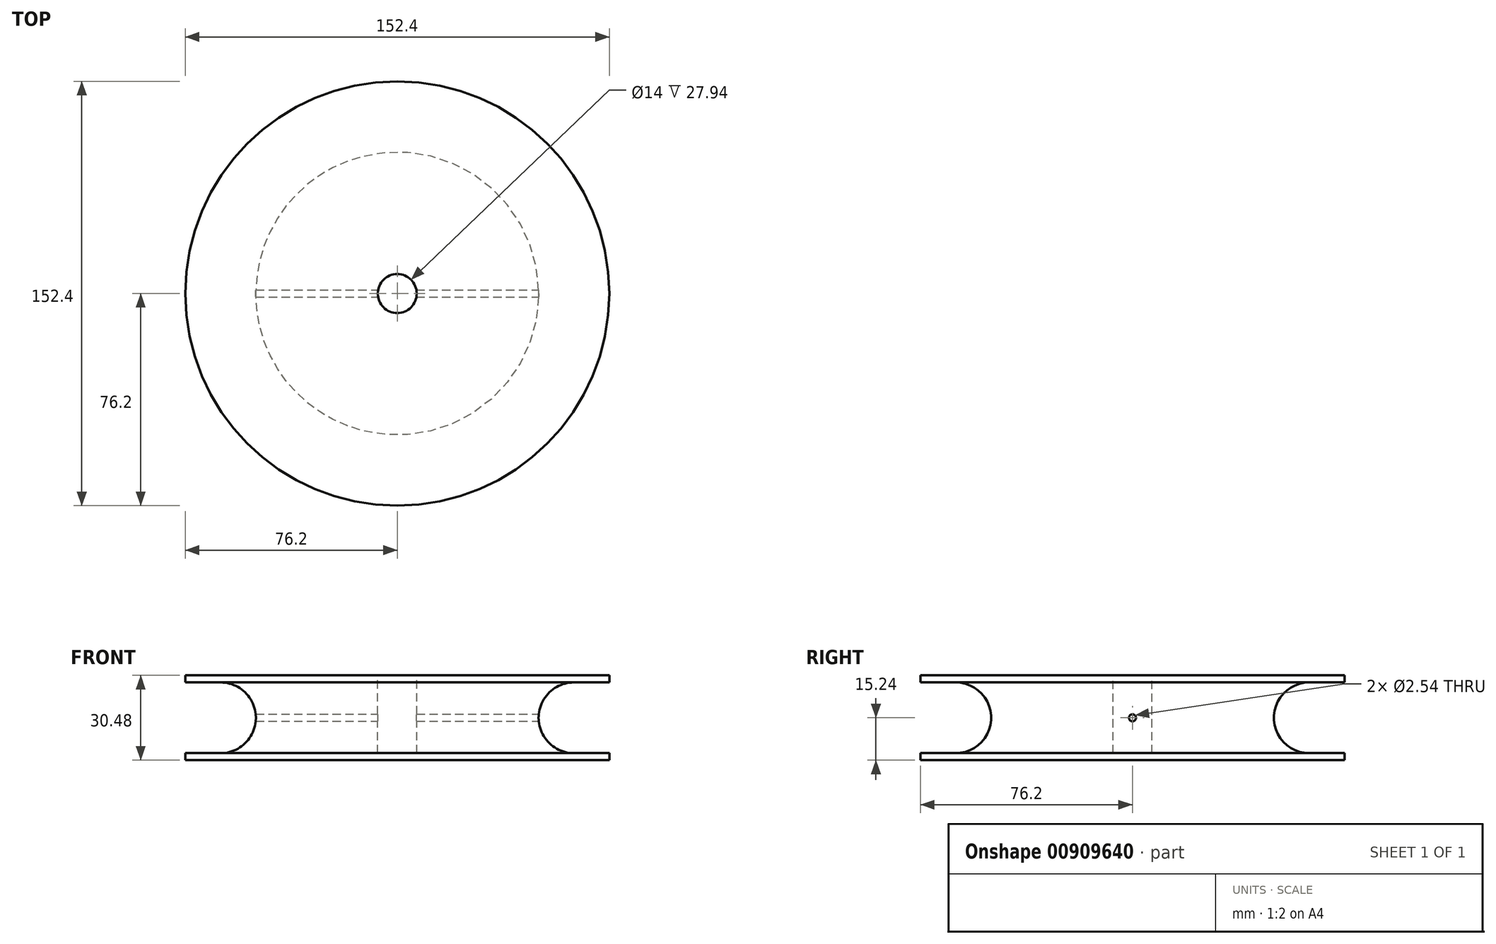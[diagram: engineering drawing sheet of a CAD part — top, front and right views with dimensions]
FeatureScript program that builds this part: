
annotation { "Feature Type Name" : "Feature", "Feature Type Description" : "" }
export const myFeature = defineFeature(function(context is Context, id is Id, definition is map)
    precondition{}
    {
        {
            var Q0;
            Q0=qCreatedBy(makeId("Top.planeOp"),FACE);
            var sketch = newSketch(context, id + "F0", { "sketchPlane" : qUnion([Q0])});
            skCircle(sketch, "E0", {"center": v(0, 0) * mm, "radius": 50.8 * mm});
            skCircle(sketch, "E1", {"center": v(0, 0) * mm, "radius": 76.2 * mm});
            skSolve(sketch);
        }
        {
            var Q0;
            Q0=makeQuery(id+"F0.imprint","IMPRINT",FACE,{"disambiguationData":[TD([[makeQuery(id+"F0.imprint","IMPRINT",EDGE,{"derivedFrom":sQuery(id+"F0.wireOp",EDGE,"E0")}),1.0]])]});
            extrude(context, id + "F1", {"entities" : qUnion([Q0]), "depth" : 30.48 * mm, "offsetDistance" : 25.4 * mm});
        }
        {
            var Q0;
            Q0=qSketchRegion(id+"F0",true);
            extrude(context, id + "F2", {"entities" : qUnion([Q0]), "operationType" : NewBodyOperationType.ADD, "depth" : 2.54 * mm, "offsetDistance" : 25.4 * mm});
        }
        {
            var Q0;
            Q0=makeQuery(id+"F1.opExtrude","CAP_FACE",FACE,{"disambiguationData":[OSD([sQuery(id+"F0.wireOp",EDGE,"E0")])],"isStart":false});
            var sketch = newSketch(context, id + "F3", { "sketchPlane" : qUnion([Q0])});
            skCircle(sketch, "E2", {"center": v(0, 0) * mm, "radius": 76.2 * mm});
            skSolve(sketch);
        }
        {
            var Q0;
            Q0=qSketchRegion(id+"F3",true);
            extrude(context, id + "F4", {"entities" : qUnion([Q0]), "operationType" : NewBodyOperationType.ADD, "depth" : -2.54 * mm, "offsetDistance" : 25.4 * mm});
        }
        {
            var Q0;
            Q0=makeQuery(id+"F1.opExtrude","SWEPT_FACE",FACE,{"disambiguationData":[OSD([sQuery(id+"F0.wireOp",EDGE,"E0")])]});
            fillet(context, id + "F5", {"entities" : qUnion([Q0]), "radius" : 12.7 * mm, "tangentPropagation" : true, "allowEdgeOverflow" : false});
        }
        {
            var Q0;
            Q0=qCreatedBy(makeId("Right.planeOp"),FACE);
            var sketch = newSketch(context, id + "F6", { "sketchPlane" : qUnion([Q0])});
            skLineSegment(sketch, "E3", {"start": v(0, 0) * mm, "end": v(0, 15.24) * mm, "construction": true});
            skCircle(sketch, "E4", {"center": v(0, 15.24) * mm, "radius": 1.27 * mm});
            skSolve(sketch);
        }
        {
            var Q0;
            Q0=qSketchRegion(id+"F6",true);
            extrude(context, id + "F7", {"entities" : qUnion([Q0]), "operationType" : NewBodyOperationType.REMOVE, "oppositeDirection" : true, "depth" : 254 * mm, "offsetDistance" : 25.4 * mm});
        }
        {
            var Q0;
            Q0=qSketchRegion(id+"F6",true);
            extrude(context, id + "F8", {"entities" : qUnion([Q0]), "operationType" : NewBodyOperationType.REMOVE, "depth" : 254 * mm, "offsetDistance" : 25.4 * mm});
        }
        {
            var Q0;
            Q0=makeQuery(id+"F4.boolean.opBoolean","MERGE",FACE,{"derivedFrom":[makeQuery(id+"F1.opExtrude","CAP_FACE",FACE,{"disambiguationData":[OSD([sQuery(id+"F0.wireOp",EDGE,"E0")])],"isStart":false}),makeQuery(id+"F4.opExtrude","CAP_FACE",FACE,{"disambiguationData":[OSD([sQuery(id+"F3.wireOp",EDGE,"E2")])],"isStart":true})]});
            var sketch = newSketch(context, id + "F9", { "sketchPlane" : qUnion([Q0])});
            skCircle(sketch, "E5", {"center": v(0, 0) * mm, "radius": 7 * mm});
            skSolve(sketch);
        }
        {
            var Q0;
            Q0=qSketchRegion(id+"F9",true);
            extrude(context, id + "F10", {"entities" : qUnion([Q0]), "operationType" : NewBodyOperationType.REMOVE, "oppositeDirection" : true, "depth" : 27.94 * mm, "offsetDistance" : 25.4 * mm});
        }
    });
